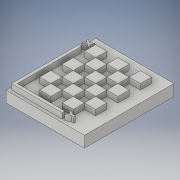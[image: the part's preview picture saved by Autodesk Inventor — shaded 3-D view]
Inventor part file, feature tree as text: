
AUTODESK INVENTOR PART (.ipt)
format: ipt  version: 2019 (Build 230136000, 136)  size: 257,024 bytes
history: native  units: in
note: dims shown in document units (in); Inventor stores cm internally (conversion verified against a paired STEP export)
features: extrude x4, sketch x4
ambient origin geometry x8: Origin, YZ Plane, XZ Plane, XY Plane, X Axis, Y Axis, Z Axis, Center Point
bodies: Solid1 (feature_tree)
feature tree (8):
  extrude  "Extrusion1"  Depth=6.2992in
  extrude  "Extrusion2"  Depth=3.1496in
  sketch  "Sketch3"  dims[d6=0.7874in d7=0.0in d8=3.937in]
  extrude  "Extrusion5"  Depth=3.937in
  extrude  "Extrusion4"  Depth=0.3937in TaperAngle=0.0deg
  sketch  "Sketch1"  dims[d0=5.5118in d1=6.2992in]
  sketch  "Sketch2"  dims[d4=2.7559in d5=3.1496in]
  sketch  "Sketch4"  dims[d9=4.7244in d10=0.3937in d11=0.0in d12=0.7874in d13=0.7874in d14=0.7874in d15=0.7874in d16=0.7874in d17=0.7874in d18=0.7874in d19=0.7874in d20=0.7874in d21=0.7874in d22=0.7874in d23=0.7874in d25=0.7874in d26=0.7874in d27=0.7874in d28=0.7874in d29=0.7874in d30=0.7874in d31=0.7874in d32=0.7874in d33=0.7874in d34=0.7874in d35=0.7874in d36=0.7874in d37=0.7874in d38=0.7874in d39=0.7874in d40=0.7874in d41=0.7874in d42=0.7874in d43=0.7874in d44=0.7874in d45=0.7874in d46=0.7874in d47=0.7874in d48=0.7874in d49=0.7874in d50=0.7874in d53=0.1969in d54=0.1969in d55=0.1969in d56=0.1969in d57=4.7244in d58=3.5433in d63=0.4823in d73=0.1969in d75=0.3937in d76=0.0in d77=0.7874in d78=0.7874in d79=0.7874in d80=0.7874in d81=0.7874in d82=0.7874in d83=0.7874in d84=0.7874in d85=0.7874in d86=0.3937in d87=0.0in d88=0.1969in d90=0.1969in]
